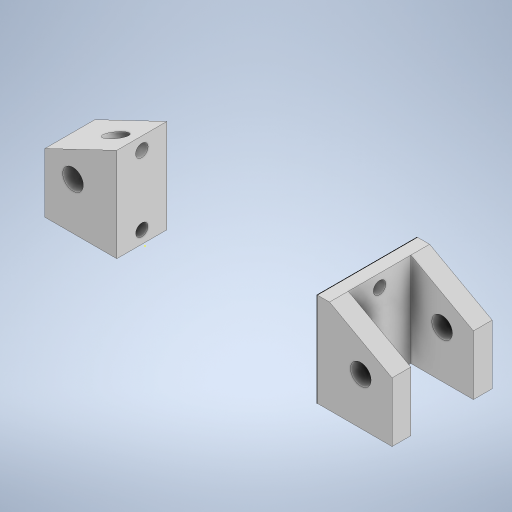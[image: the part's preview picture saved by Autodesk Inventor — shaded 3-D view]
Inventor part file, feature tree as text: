
AUTODESK INVENTOR PART (.ipt)
format: ipt  version: 2024 (Build 280153000, 153)  size: 379,392 bytes
history: native  units: mm
features: sketch x17, extrude x13, chamfer x3, plane x1, split x1, move_body x1
ambient origin geometry x8: Origin, YZ Plane, XZ Plane, XY Plane, X Axis, Y Axis, Z Axis, Center Point
bodies: Solid1 (feature_tree), Solid2 (feature_tree), Solid3 (feature_tree)
feature tree (36):
  extrude  "Extrusion1"  Depth=16.0mm
  sketch  "Sketch2"  dims[d2=15.0mm d3=0.0mm d4=10.0mm]
  extrude  "Extrusion2"  Depth=10.0mm
  chamfer  "Chamfer1"  Distance=21.25mm
  extrude  "Extrusion3"  Depth=10.0mm TaperAngle=0.0deg
  extrude  "Extrusion4"  Depth=11.5mm TaperAngle=0.0deg
  extrude  "Extrusion5"  Depth=1.0mm TaperAngle=0.0deg
  chamfer  "Chamfer2"  Distance=11.5mm Angle=45.0deg
  sketch  "Sketch6"  dims[d14=7.0mm d15=11.5mm d16=0.0mm]
  extrude  "Extrusion6"  Depth=9.0mm
  extrude  "Extrusion7"  Depth=11.5mm TaperAngle=0.0deg
  chamfer  "Chamfer3"  Distance=11.5mm Angle=45.0deg
  sketch  "Sketch9"  dims[d26=3.3mm d27=45.25mm d28=0.0mm d29=11.5mm d30=5.5mm d31=45.0deg]
  extrude  "Extrusion8"  Depth=2.0mm TaperAngle=0.0deg
  extrude  "Extrusion9"  Depth=9.0mm TaperAngle=0.0deg
  extrude  "Extrusion10"  Depth=13.0mm TaperAngle=0.0deg
  sketch  "Sketch13"  dims[d43=24.0mm d44=21.0mm d45=0.0mm]
  extrude  "Extrusion11"  Depth=21.0mm TaperAngle=0.0deg
  extrude  "Extrusion12"  TaperAngle=0.0deg  [1 undecoded]
  extrude  "Extrusion13"  Depth=0.872665mm
  plane  "Work Plane1"
  split  "Split1"
  move_body  "Move Body1"
  sketch  "Sketch17"  dims[d53=0.872665mm]
  sketch  "Sketch1"  dims[d0=36.0mm d1=16.0mm]
  sketch  "Sketch3"  dims[d5=10.0mm]
  sketch  "Sketch4"  dims[d6=3.3mm d7=21.25mm d8=0.0mm]
  sketch  "Sketch5"  dims[d9=10.0mm d10=5.5mm d11=45.0deg d12=10.0mm d13=0.0mm]
  sketch  "Sketch7"  dims[d17=3.3mm d18=1.0mm d19=0.0mm d20=6.0mm d21=11.5mm d22=45.0deg]
  sketch  "Sketch8"  dims[d23=15.0mm d24=0.0mm d25=9.0mm]
  sketch  "Sketch10"  dims[d32=2.0mm d33=65.75mm d34=0.0mm]
  sketch  "Sketch11"  dims[d35=0.5mm d36=0.0mm d37=9.0mm d38=0.0mm]
  sketch  "Sketch12"  dims[d39=0.5mm d40=0.0mm d41=13.0mm d42=0.0mm]
  sketch  "Sketch14"  dims[d46=12.25mm d47=-12.0mm d48=0.0mm d49=0.0mm]
  sketch  "Sketch15"  dims[d50=0.5mm d51=0.872665mm]
  sketch  "Sketch16"  dims[d52=0.5mm]
note: 1 required parameter value undecoded (feature->parameter linkage not recoverable at this tier; creation-order binding heuristic only, values carry confidence <= 0.55)
